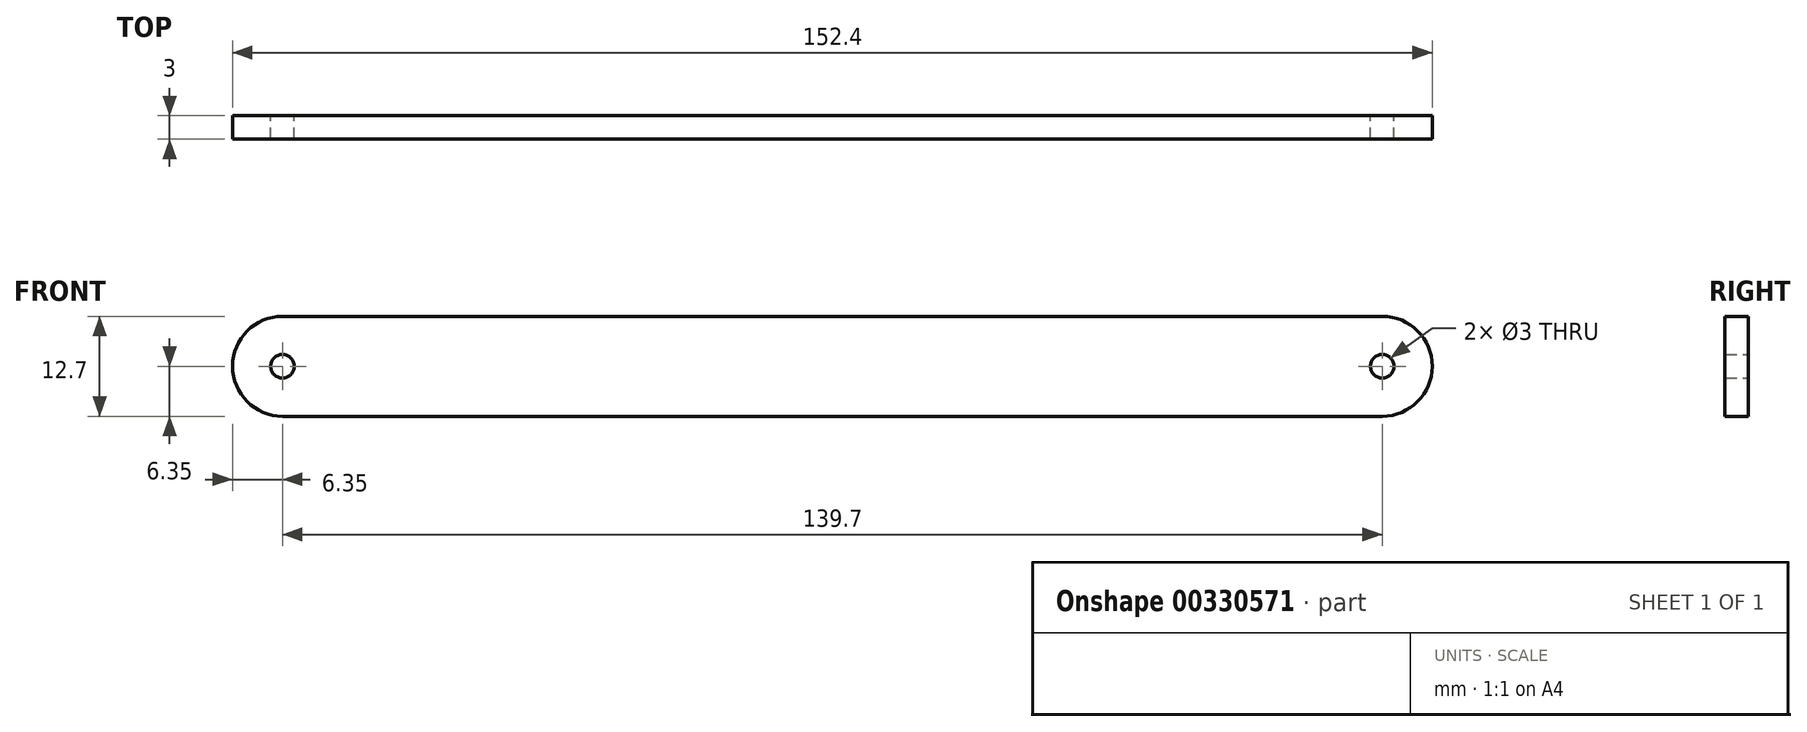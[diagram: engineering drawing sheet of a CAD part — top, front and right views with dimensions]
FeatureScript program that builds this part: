
annotation { "Feature Type Name" : "Feature", "Feature Type Description" : "" }
export const myFeature = defineFeature(function(context is Context, id is Id, definition is map)
    precondition{}
    {
        {
            var Q0;
            Q0=qCreatedBy(makeId("Front.planeOp"),FACE);
            var sketch = newSketch(context, id + "F0", { "sketchPlane" : qUnion([Q0])});
            skLineSegment(sketch, "E0", {"start": v(-69.85, 6.35) * mm, "end": v(69.85, 6.35) * mm});
            skLineSegment(sketch, "E1.MirrorCS", {"start": v(-69.85, -6.35) * mm, "end": v(69.85, -6.35) * mm});
            skArc(sketch, "E2", {"start": v(-69.85, 6.35) * mm, "mid": v(-76.2, 0) * mm, "end": v(-69.85, -6.35) * mm});
            skArc(sketch, "E3", {"start": v(69.85, 6.35) * mm, "mid": v(76.2, 0) * mm, "end": v(69.85, -6.35) * mm});
            skCircle(sketch, "E4", {"center": v(-69.85, 0) * mm, "radius": 1.5 * mm});
            skCircle(sketch, "E5", {"center": v(69.85, 0) * mm, "radius": 1.5 * mm});
            skSolve(sketch);
        }
        {
            var Q0;
            Q0=makeQuery(id+"F0.imprint","IMPRINT",FACE,{"disambiguationData":[TD([[makeQuery(id+"F0.imprint","IMPRINT",EDGE,{"derivedFrom":sQuery(id+"F0.wireOp",EDGE,"E0")}),-1.0]])]});
            extrude(context, id + "F1", {"entities" : qUnion([Q0]), "depth" : 3 * mm});
        }
    });
